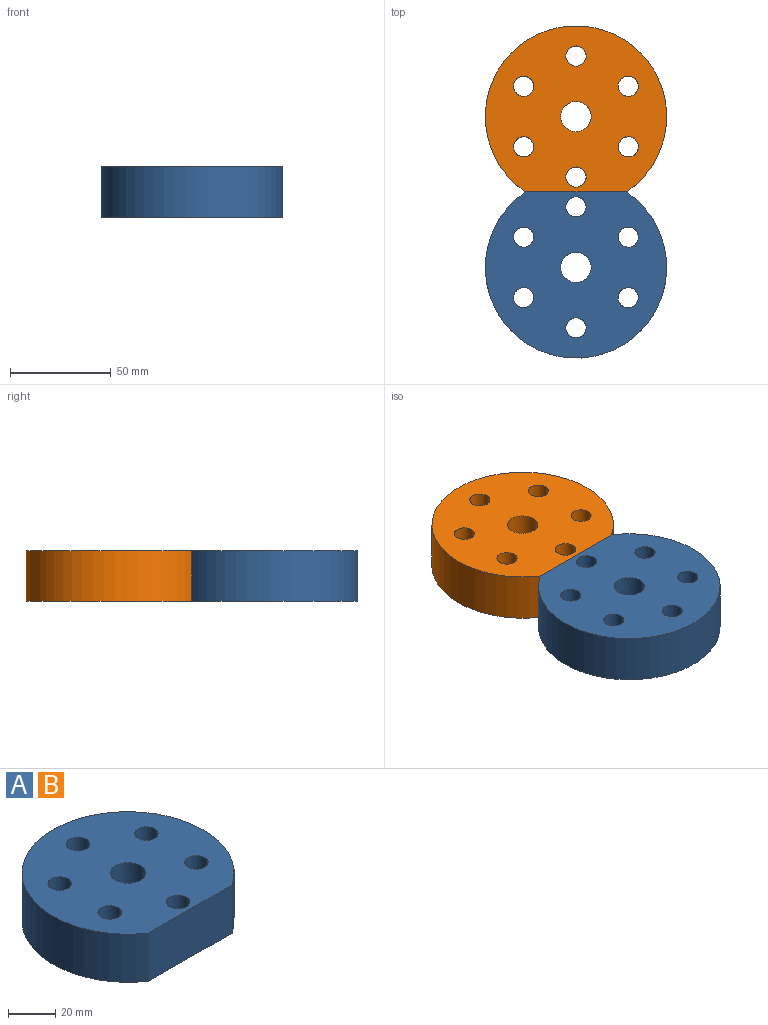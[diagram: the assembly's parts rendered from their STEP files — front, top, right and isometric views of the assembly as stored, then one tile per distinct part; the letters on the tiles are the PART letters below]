
ASSEMBLY  parts=2 mates=1
PART A: 11 faces, bbox 90x82.4x25 mm
  f0: plane 90x82.42mm, normal (0,0,1), area 5456.4mm2, adj f2,f3,f4,f5,f6,f7,f8,f9
  f1: plane 90x82.42mm, normal (0,0,-1), area 5456.4mm2, adj f2,f3,f4,f5,f6,f7,f8,f9
  f2: cylinder r=45mm len=90mm, axis (0,0,-1), area 5743.3mm2, adj f0,f1,f10
  f3: cylinder r=7.5mm len=25mm, axis (0,0,-1), area 1178.1mm2, adj f0,f1
  f4: cylinder r=5mm len=25mm, axis (0,0,-1), area 785.4mm2, adj f0,f1
  f5: cylinder r=5mm len=25mm, axis (0,0,-1), area 785.4mm2, adj f0,f1
  f6: cylinder r=5mm len=25mm, axis (0,0,-1), area 785.4mm2, adj f0,f1
  f7: cylinder r=5mm len=25mm, axis (0,0,-1), area 785.4mm2, adj f0,f1
  f8: cylinder r=5mm len=25mm, axis (0,0,-1), area 785.4mm2, adj f0,f1
  f9: cylinder r=5mm len=25mm, axis (0,0,-1), area 785.4mm2, adj f0,f1
  f10: plane 50x25mm, normal (0,-1,0), area 1250mm2, adj f0,f1,f2
PART B: same geometry as A
PLACE A rot(axis=(-1,0,0),180deg) t=(28.17,-110.42,-3.63)mm
PLACE B rot(axis=(0.27,-0.42,-0.87),0deg) t=(28.17,-35.58,-28.63)mm
MATE fastened A.f10 <-> B.f10  axis (0,1,0) through (28.17,-73,-16.13)mm
